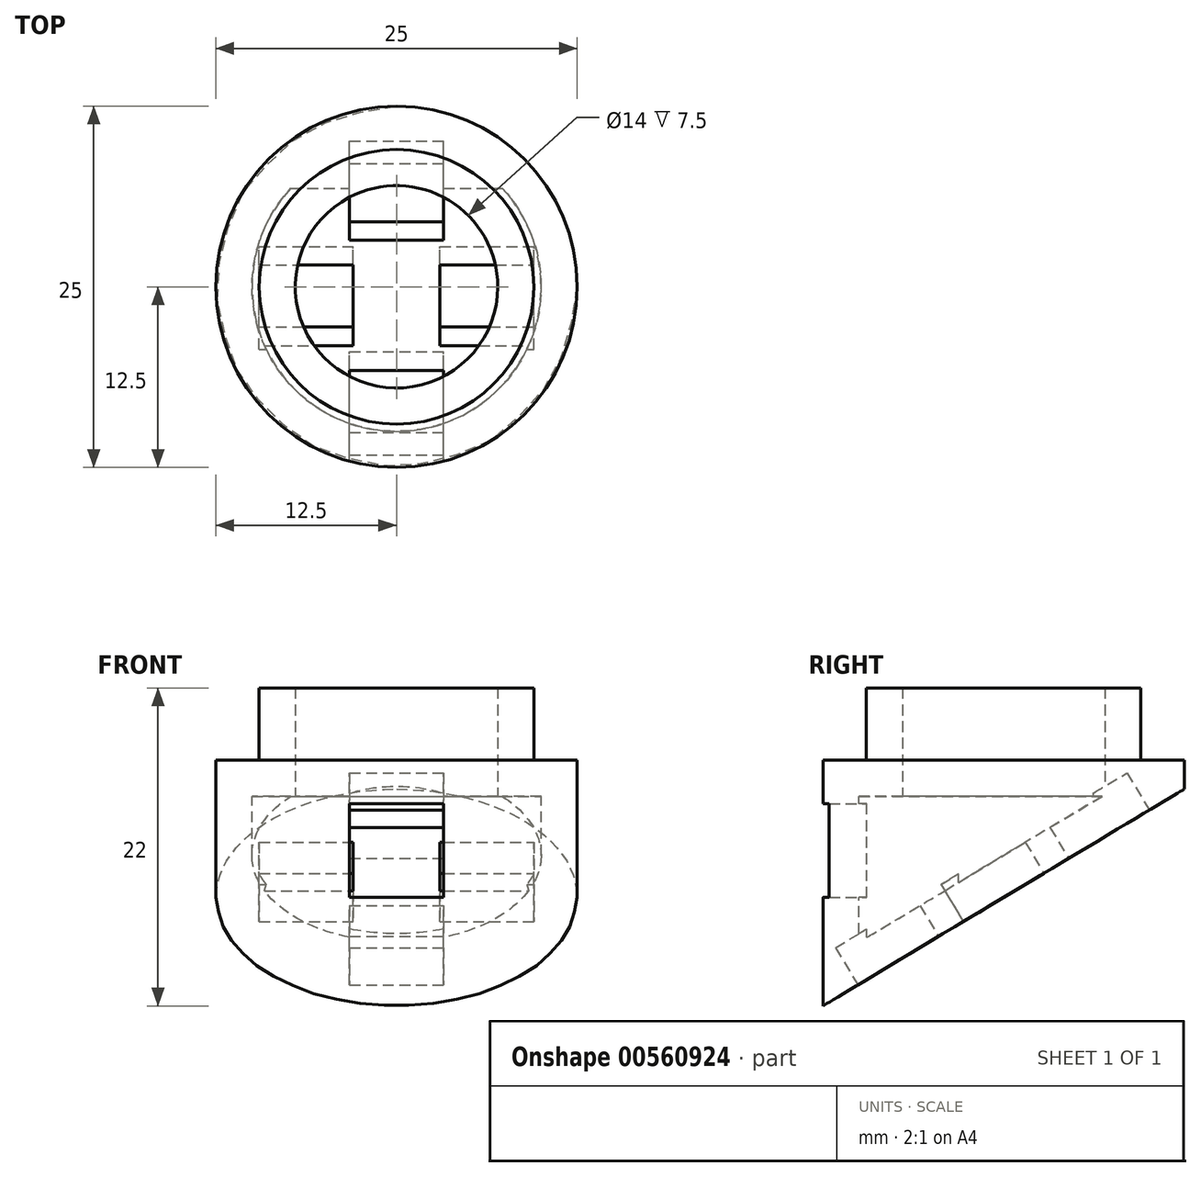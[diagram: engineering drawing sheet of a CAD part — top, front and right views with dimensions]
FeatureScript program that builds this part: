
annotation { "Feature Type Name" : "Feature", "Feature Type Description" : "" }
export const myFeature = defineFeature(function(context is Context, id is Id, definition is map)
    precondition{}
    {
        {
            var Q0;
            Q0=qCreatedBy(makeId("Top.planeOp"),FACE);
            var sketch = newSketch(context, id + "F0", { "sketchPlane" : qUnion([Q0])});
            skCircle(sketch, "E0", {"center": v(0, 0) * mm, "radius": 9.5 * mm});
            skCircle(sketch, "E1", {"center": v(0, 0) * mm, "radius": 12.5 * mm});
            skSolve(sketch);
        }
        {
            var Q0;
            Q0=makeQuery(id+"F0.imprint","IMPRINT",FACE,{"disambiguationData":[TD([[makeQuery(id+"F0.imprint","IMPRINT",EDGE,{"derivedFrom":sQuery(id+"F0.wireOp",EDGE,"E0")}),-1.0]])]});
            var Q1;
            Q1=makeQuery(id+"F0.imprint","IMPRINT",FACE,{"disambiguationData":[TD([[makeQuery(id+"F0.imprint","IMPRINT",EDGE,{"derivedFrom":sQuery(id+"F0.wireOp",EDGE,"E0")}),1.0]])]});
            extrude(context, id + "F1", {"entities" : qUnion([Q0, Q1]), "oppositeDirection" : true, "depth" : 17 * mm, "offsetDistance" : 25 * mm});
        }
        {
            var Q0;
            Q0=makeQuery(id+"F0.imprint","IMPRINT",FACE,{"disambiguationData":[TD([[makeQuery(id+"F0.imprint","IMPRINT",EDGE,{"derivedFrom":sQuery(id+"F0.wireOp",EDGE,"E0")}),1.0]])]});
            extrude(context, id + "F2", {"entities" : qUnion([Q0]), "operationType" : NewBodyOperationType.ADD, "depth" : 5 * mm, "offsetDistance" : 25 * mm});
        }
        {
            var Q0;
            Q0=qCreatedBy(makeId("Right.planeOp"),FACE);
            var sketch = newSketch(context, id + "F3", { "sketchPlane" : qUnion([Q0])});
            skLineSegment(sketch, "E2", {"start": v(12.5, -2) * mm, "end": v(-12.5, -17) * mm});
            skLineSegment(sketch, "E3", {"start": v(-12.5, -17) * mm, "end": v(12.5, -17) * mm});
            skLineSegment(sketch, "E4", {"start": v(12.5, -17) * mm, "end": v(12.5, -2) * mm});
            skSolve(sketch);
        }
        {
            var Q0;
            Q0=makeQuery(id+"F3.imprint","IMPRINT",FACE,{"disambiguationData":[TD([[makeQuery(id+"F3.imprint","IMPRINT",EDGE,{"derivedFrom":sQuery(id+"F3.wireOp",EDGE,"E2")}),1.0]])]});
            extrude(context, id + "F4", {"entities" : qUnion([Q0]), "operationType" : NewBodyOperationType.REMOVE, "depth" : 25 * mm, "offsetDistance" : 25 * mm, "symmetric" : true});
        }
        {
            var Q0;
            Q0=makeQuery(id+"F2.opExtrude","CAP_FACE",FACE,{"disambiguationData":[OSD([sQuery(id+"F0.wireOp",EDGE,"E0")])],"isStart":false});
            shell(context, id + "F5", {"entities" : qUnion([Q0]), "thickness" : 2.5 * mm});
        }
        {
            var Q0;
            Q0=makeQuery(id+"F4.boolean.opBoolean","COPY",FACE,{"derivedFrom":makeQuery(id+"F4.opExtrude","SWEPT_FACE",FACE,{"disambiguationData":[OSD([sQuery(id+"F3.wireOp",EDGE,"E2")])]})});
            var sketch = newSketch(context, id + "F6", { "sketchPlane" : qUnion([Q0])});
            skLineSegment(sketch, "E5.bottom", {"start": v(-3.25, 16.64) * mm, "end": v(3.25, 16.64) * mm});
            skLineSegment(sketch, "E5.top", {"start": v(-3.25, 10.14) * mm, "end": v(3.25, 10.14) * mm});
            skLineSegment(sketch, "E5.left", {"start": v(-3.25, 16.64) * mm, "end": v(-3.25, 10.14) * mm});
            skLineSegment(sketch, "E5.right", {"start": v(3.25, 16.64) * mm, "end": v(3.25, 10.14) * mm});
            skLineSegment(sketch, "E6.bottom", {"start": v(-9.5, 8.14) * mm, "end": v(-3, 8.14) * mm});
            skLineSegment(sketch, "E6.top", {"start": v(-9.5, 1.64) * mm, "end": v(-3, 1.64) * mm});
            skLineSegment(sketch, "E6.left", {"start": v(-9.5, 8.14) * mm, "end": v(-9.5, 1.64) * mm});
            skLineSegment(sketch, "E6.right", {"start": v(-3, 8.14) * mm, "end": v(-3, 1.64) * mm});
            skLineSegment(sketch, "E7.bottom", {"start": v(3, 8.14) * mm, "end": v(9.5, 8.14) * mm});
            skLineSegment(sketch, "E7.top", {"start": v(3, 1.64) * mm, "end": v(9.5, 1.64) * mm});
            skLineSegment(sketch, "E7.left", {"start": v(3, 8.14) * mm, "end": v(3, 1.64) * mm});
            skLineSegment(sketch, "E7.right", {"start": v(9.5, 8.14) * mm, "end": v(9.5, 1.64) * mm});
            skLineSegment(sketch, "E8.bottom", {"start": v(-3.25, -0.36) * mm, "end": v(3.25, -0.36) * mm});
            skLineSegment(sketch, "E8.top", {"start": v(-3.25, -6.86) * mm, "end": v(3.25, -6.86) * mm});
            skLineSegment(sketch, "E8.left", {"start": v(-3.25, -0.36) * mm, "end": v(-3.25, -6.86) * mm});
            skLineSegment(sketch, "E8.right", {"start": v(3.25, -0.36) * mm, "end": v(3.25, -6.86) * mm});
            skSolve(sketch);
        }
        {
            var Q0;
            Q0=makeQuery(id+"F6.imprint","IMPRINT",FACE,{"disambiguationData":[TD([[makeQuery(id+"F6.imprint","IMPRINT",EDGE,{"derivedFrom":sQuery(id+"F6.wireOp",EDGE,"E6.bottom")}),-1.0]])]});
            var Q1;
            Q1=makeQuery(id+"F6.imprint","IMPRINT",FACE,{"disambiguationData":[TD([[makeQuery(id+"F6.imprint","IMPRINT",EDGE,{"derivedFrom":sQuery(id+"F6.wireOp",EDGE,"E7.bottom")}),-1.0]])]});
            var Q2;
            Q2=makeQuery(id+"F6.imprint","IMPRINT",FACE,{"disambiguationData":[TD([[makeQuery(id+"F6.imprint","IMPRINT",EDGE,{"derivedFrom":sQuery(id+"F6.wireOp",EDGE,"E8.bottom")}),-1.0]])]});
            var Q3;
            Q3=makeQuery(id+"F6.imprint","IMPRINT",FACE,{"disambiguationData":[TD([[makeQuery(id+"F6.imprint","IMPRINT",EDGE,{"derivedFrom":sQuery(id+"F6.wireOp",EDGE,"E5.bottom")}),-1.0]])]});
            extrude(context, id + "F7", {"entities" : qUnion([Q0, Q1, Q2, Q3]), "operationType" : NewBodyOperationType.REMOVE, "oppositeDirection" : true, "depth" : 3 * mm, "offsetDistance" : 25 * mm});
        }
        {
            var Q0;
            Q0=qCreatedBy(makeId("Front.planeOp"),FACE);
            var sketch = newSketch(context, id + "F8", { "sketchPlane" : qUnion([Q0])});
            skLineSegment(sketch, "E9.bottom", {"start": v(-3.25, -3) * mm, "end": v(3.25, -3) * mm});
            skLineSegment(sketch, "E9.top", {"start": v(-3.25, -9.5) * mm, "end": v(3.25, -9.5) * mm});
            skLineSegment(sketch, "E9.left", {"start": v(-3.25, -3) * mm, "end": v(-3.25, -9.5) * mm});
            skLineSegment(sketch, "E9.right", {"start": v(3.25, -3) * mm, "end": v(3.25, -9.5) * mm});
            skSolve(sketch);
        }
        {
            var Q0;
            Q0=makeQuery(id+"F8.imprint","IMPRINT",FACE,{"disambiguationData":[TD([[makeQuery(id+"F8.imprint","IMPRINT",EDGE,{"derivedFrom":sQuery(id+"F8.wireOp",EDGE,"E9.bottom")}),-1.0]])]});
            extrude(context, id + "F9", {"entities" : qUnion([Q0]), "operationType" : NewBodyOperationType.REMOVE, "depth" : 20 * mm, "offsetDistance" : 25 * mm, "hasSecondDirection" : true, "secondDirectionOppositeDirection" : false, "secondDirectionDepth" : 7 * mm});
        }
    });
